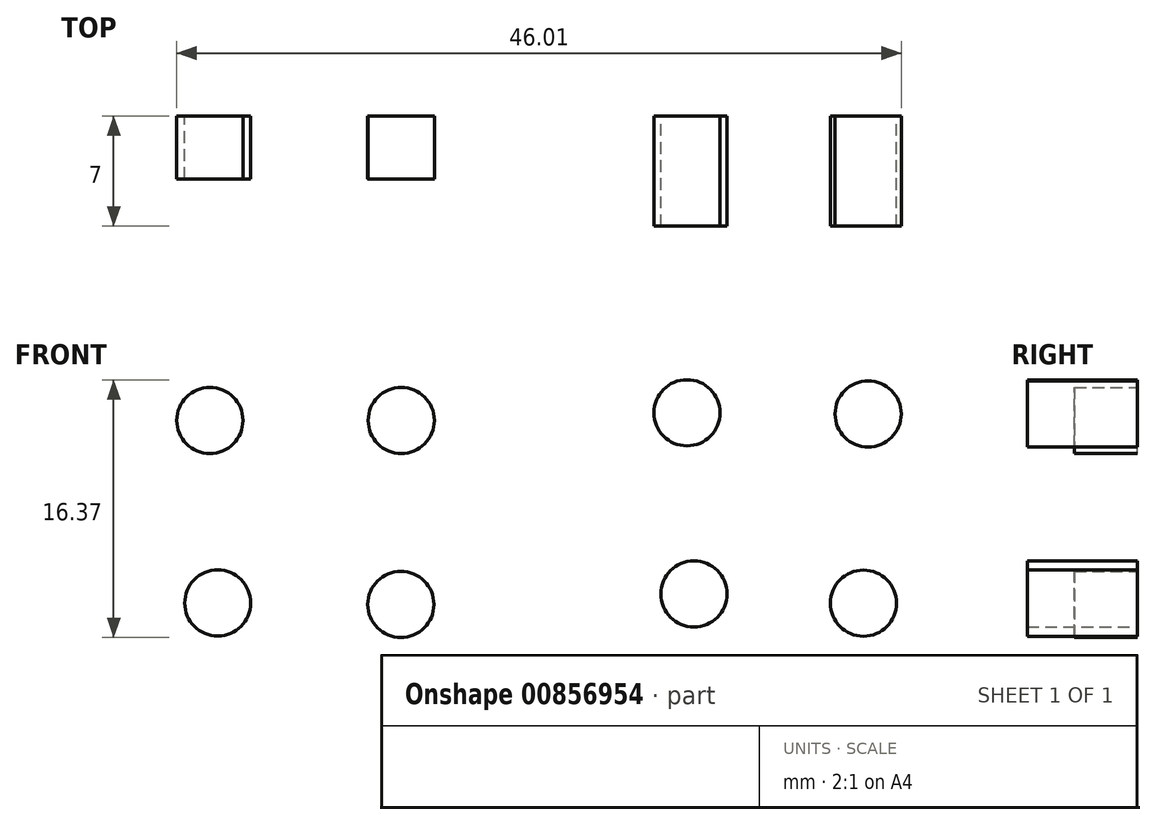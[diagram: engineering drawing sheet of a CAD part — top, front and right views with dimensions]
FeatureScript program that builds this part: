
annotation { "Feature Type Name" : "Feature", "Feature Type Description" : "" }
export const myFeature = defineFeature(function(context is Context, id is Id, definition is map)
    precondition{}
    {
        {
            var Q0;
            Q0=qCreatedBy(makeId("Front.planeOp"),FACE);
            var sketch = newSketch(context, id + "F0", { "sketchPlane" : qUnion([Q0])});
            skCircle(sketch, "E0", {"center": v(0, 0) * mm, "radius": 2.1 * mm});
            skCircle(sketch, "E1", {"center": v(0, 0) * mm, "radius": 4.7 * mm});
            skCircle(sketch, "E2", {"center": v(-11.63, 0.09) * mm, "radius": 2.1 * mm});
            skCircle(sketch, "E3", {"center": v(-11.63, 0.09) * mm, "radius": 4.7 * mm});
            skCircle(sketch, "E4", {"center": v(-12.13, 11.69) * mm, "radius": 2.1 * mm});
            skCircle(sketch, "E5", {"center": v(-12.13, 11.69) * mm, "radius": 4.7 * mm});
            skCircle(sketch, "E6", {"center": v(0.03, 11.69) * mm, "radius": 2.1 * mm});
            skCircle(sketch, "E7", {"center": v(0.03, 11.69) * mm, "radius": 4.7 * mm});
            skCircle(sketch, "E8", {"center": v(18.17, 12.17) * mm, "radius": 2.1 * mm});
            skCircle(sketch, "E9", {"center": v(18.17, 12.17) * mm, "radius": 4.7 * mm});
            skCircle(sketch, "E10", {"center": v(18.61, 0.66) * mm, "radius": 2.1 * mm});
            skCircle(sketch, "E11", {"center": v(18.61, 0.66) * mm, "radius": 4.7 * mm});
            skCircle(sketch, "E12", {"center": v(29.38, 0.08) * mm, "radius": 2.1 * mm});
            skCircle(sketch, "E13", {"center": v(29.38, 0.08) * mm, "radius": 4.7 * mm});
            skCircle(sketch, "E14", {"center": v(29.68, 12.1) * mm, "radius": 2.1 * mm});
            skCircle(sketch, "E15", {"center": v(29.68, 12.1) * mm, "radius": 4.7 * mm});
            skSolve(sketch);
        }
        {
            var Q0;
            Q0=makeQuery(id+"F0.imprint","IMPRINT",FACE,{"disambiguationData":[TD([[makeQuery(id+"F0.imprint","IMPRINT",EDGE,{"derivedFrom":sQuery(id+"F0.wireOp",EDGE,"E8")}),1.0]])]});
            var Q1;
            Q1=makeQuery(id+"F0.imprint","IMPRINT",FACE,{"disambiguationData":[TD([[makeQuery(id+"F0.imprint","IMPRINT",EDGE,{"derivedFrom":sQuery(id+"F0.wireOp",EDGE,"E14")}),1.0]])]});
            var Q2;
            Q2=makeQuery(id+"F0.imprint","IMPRINT",FACE,{"disambiguationData":[TD([[makeQuery(id+"F0.imprint","IMPRINT",EDGE,{"derivedFrom":sQuery(id+"F0.wireOp",EDGE,"E12")}),1.0]])]});
            var Q3;
            Q3=makeQuery(id+"F0.imprint","IMPRINT",FACE,{"disambiguationData":[TD([[makeQuery(id+"F0.imprint","IMPRINT",EDGE,{"derivedFrom":sQuery(id+"F0.wireOp",EDGE,"E10")}),1.0]])]});
            extrude(context, id + "F1", {"entities" : qUnion([Q0, Q1, Q2, Q3]), "depth" : 7 * mm, "offsetDistance" : 25 * mm});
        }
        {
            var Q0;
            Q0=makeQuery(id+"F0.imprint","IMPRINT",FACE,{"disambiguationData":[TD([[makeQuery(id+"F0.imprint","IMPRINT",EDGE,{"derivedFrom":sQuery(id+"F0.wireOp",EDGE,"E4")}),1.0]])]});
            var Q1;
            Q1=makeQuery(id+"F0.imprint","IMPRINT",FACE,{"disambiguationData":[TD([[makeQuery(id+"F0.imprint","IMPRINT",EDGE,{"derivedFrom":sQuery(id+"F0.wireOp",EDGE,"E6")}),1.0]])]});
            var Q2;
            Q2=makeQuery(id+"F0.imprint","IMPRINT",FACE,{"disambiguationData":[TD([[makeQuery(id+"F0.imprint","IMPRINT",EDGE,{"derivedFrom":sQuery(id+"F0.wireOp",EDGE,"E0")}),1.0]])]});
            var Q3;
            Q3=makeQuery(id+"F0.imprint","IMPRINT",FACE,{"disambiguationData":[TD([[makeQuery(id+"F0.imprint","IMPRINT",EDGE,{"derivedFrom":sQuery(id+"F0.wireOp",EDGE,"E2")}),1.0]])]});
            extrude(context, id + "F2", {"entities" : qUnion([Q0, Q1, Q2, Q3]), "depth" : 4 * mm, "offsetDistance" : 25 * mm});
        }
    });
